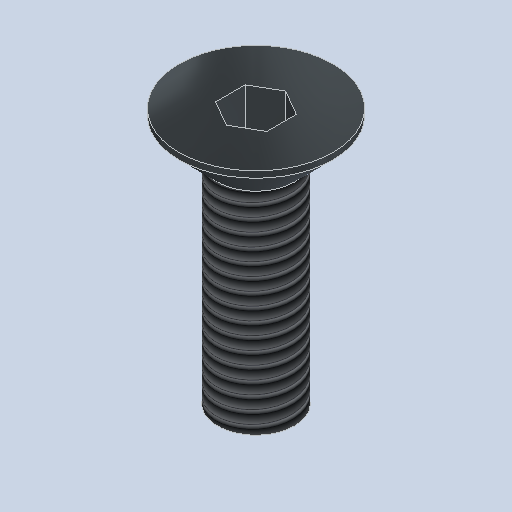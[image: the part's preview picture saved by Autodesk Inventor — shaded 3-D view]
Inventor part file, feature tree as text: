
AUTODESK INVENTOR PART (.ipt)
format: ipt  version: 2023 (Build 270158030, 158C)  size: 171,008 bytes
history: native  units: mm
features: extrude x3, sketch x3, other x1, thread x1, chamfer x1
ambient origin geometry x8: Origin, YZ Plane, XZ Plane, XY Plane, X Axis, Y Axis, Z Axis, Center Point
bodies: Body1 (feature_tree)
feature tree (9):
  other  "ソリッド1"
  extrude  "押し出し1"  Depth=3.0mm
  thread  "ねじ1"
  extrude  "押し出し2"  Depth=10.0mm TaperAngle=0.0deg
  chamfer  "面取り1"  Distance=10.0mm
  extrude  "押し出し3"  Depth=6.0mm
  sketch  "スケッチ1"
  sketch  "スケッチ2"
  sketch  "スケッチ3"
